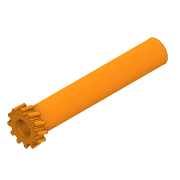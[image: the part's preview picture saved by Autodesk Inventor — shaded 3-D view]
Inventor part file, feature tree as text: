
AUTODESK INVENTOR PART (.ipt)
format: ipt  version: 2020 (Build 240168000, 168)  size: 315,392 bytes
history: native  units: in
note: dims shown in document units (in); Inventor stores cm internally (conversion verified against a paired STEP export)
features: sketch x3, extrude x1, plane x1, sweep x1, other x1
ambient origin geometry x8: Origin, YZ Plane, XZ Plane, XY Plane, X Axis, Y Axis, Z Axis, Center Point
bodies: Solid1 (feature_tree)
feature tree (7):
  extrude  "Extrusion1"  Depth=0.315in
  plane  "Work Plane1"
  sweep  "Sweep1"
  sketch  "Sketch1"  dims[d0=0.4724in d1=0.315in]
  sketch  "Sketch3"  dims[d2=2.9921in d3=0.0in d7=-0.1969in d8=0.7087in d9=0.0866in d10=0.0787in d11=0.0787in d12=0.0787in d13=4.7244in d15=360.0deg d17=0.1969in d18=0.0118in d19=0.535in d20=0.0in d21=0.0in d22=0.0in d23=0.5in d24=0.0344in d25=0.5in d26=0.0344in]
  sketch  "3D Sketch1"
  other  "Helical Curve1"
